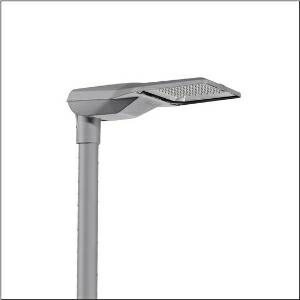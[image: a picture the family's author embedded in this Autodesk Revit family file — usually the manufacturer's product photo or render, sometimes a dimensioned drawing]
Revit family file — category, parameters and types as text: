
# Revit family: streetlight_sl_21_midi___pc-l_5xe7f43a08mb_85ee
name_source: partatom
category: Lighting Fixtures
units: mm (PartAtom-declared; Revit-internal decimal feet)

## family parameters
Cut with Voids When Loaded = No
Host = Face
Light Source = No
Part Type = Normal
Room Calculation Point = No
Round Connector Dimension = Use Diameter
Shared = No

## types (1)
- --- (1 x LED, 19200 lm, 147 W, 4000K)
    Apparent Load = 147 VA
    CIE Flux Codes = 38 78 98 100 100
    Color Rendering = 70
    Color Temperature = 4000K
    Default Elevation = 1800 mm
    Description = Streetlight SL 21 midi, mast luminaire, primary light control with lens, of PMMA, primary optical cover: cover, of toughened safety glass, transparent, light distribution: PC-L, light emission: direct distribution, primary light characteristic: asymmetric, left, installation type: post-top, side-entry, LED, 3G 1.5mm², High Power LED, rated luminous flux: 19.200lm, luminous efficacy: 131lm/W, light colour: 740, colour temperature: 4000K, control gear: Easy, control: overheat protection, constant luminous flux control, time-dependent luminous flux control, flexible luminous flux parameterisation, mains connection: 220..240V, AC, 50/60Hz, connection cable pre-assembled, cable length: 12,5m, wiring characteristics: H07RN-F, start of lifetime: 147W, end of service life: 155W, reduction: 64W, luminaire housing, of diecast aluminium, powder-coated, Siteco® metallic grey (DB 702S), corrosivity category C5 mid according to DIN EN ISO 12944, please order mast flange separately, inclination adjustable: 0°, 5°, 10°, 15°, sealing non-destructively replaceable, multi-level sealing system, length: 644mm, width: 335mm, height: 110mm, mast flange for spigot size: 42mm (side-entry): 5XC10008XM4, 60/48mm (side-entry/post-top): 5XC10108XM2, 76/60mm (side-entry/post-top): 5XC10108XM1, mounting height: 4..8m, protection rating (complete): IP66, insulation class (complete): insulation class II (safety insulation), certification: CE, ENEC, ENEC+, VDE, impact resistance: IK10, permissible operating ambient temperature for outdoor applications: -40..+50°C, standard-compliant lighting for roads and squares, packaging unit: 1 piece

Light Distribution: PC-L
    Height = 111 mm
    Lamp = 1 x LED
    Lamp Light Flux = 19200 lm
    Lamp Power = 147 W
    Lamp count = 1
    Length = 644 mm
    Luminous efficacy = 131 lm/W
    Manufacturer = Siteco
    ModVariant = No
    Model = 5XE7F43A08MB
    Number of Poles = 1
    OnlyDefault = Yes
    Power Factor = 1
    Product Name = Streetlight SL 21 midi | PC-L
    Product group = mast luminaire | pylon top
    ProductGroupID = 6100
    Protection Class = Protection class II
    Protection Degree = IP 66
    RLX_Detail_Level = 1
    RLX_Emergency_Light_Flux = 0 lm
    RLX_Emergency_Type = 0
    RLX_Emergency_Type_DB = No
    RlxData = <blob elided: 29353 chars, md5=8b9f4cee>
    Socket = socket
    Standby Power = 0 W
    System Light Flux = 19200 lm
    System Power = 147 W
    Type Comments = factory setting: luminous flux: 100 % | Output Level: 100 % | 750 mA
    Type Image = l_1004298.jpg
    URL = http://relux.com
    VarID = @adj_085649
    Voltage = 0 V
    Weight = 0.00 kg
    Width = 336 mm

## geometry (parser evidence)
native form markers: Blend x4, Sweep x9
no freeform markers — native parametric forms only
